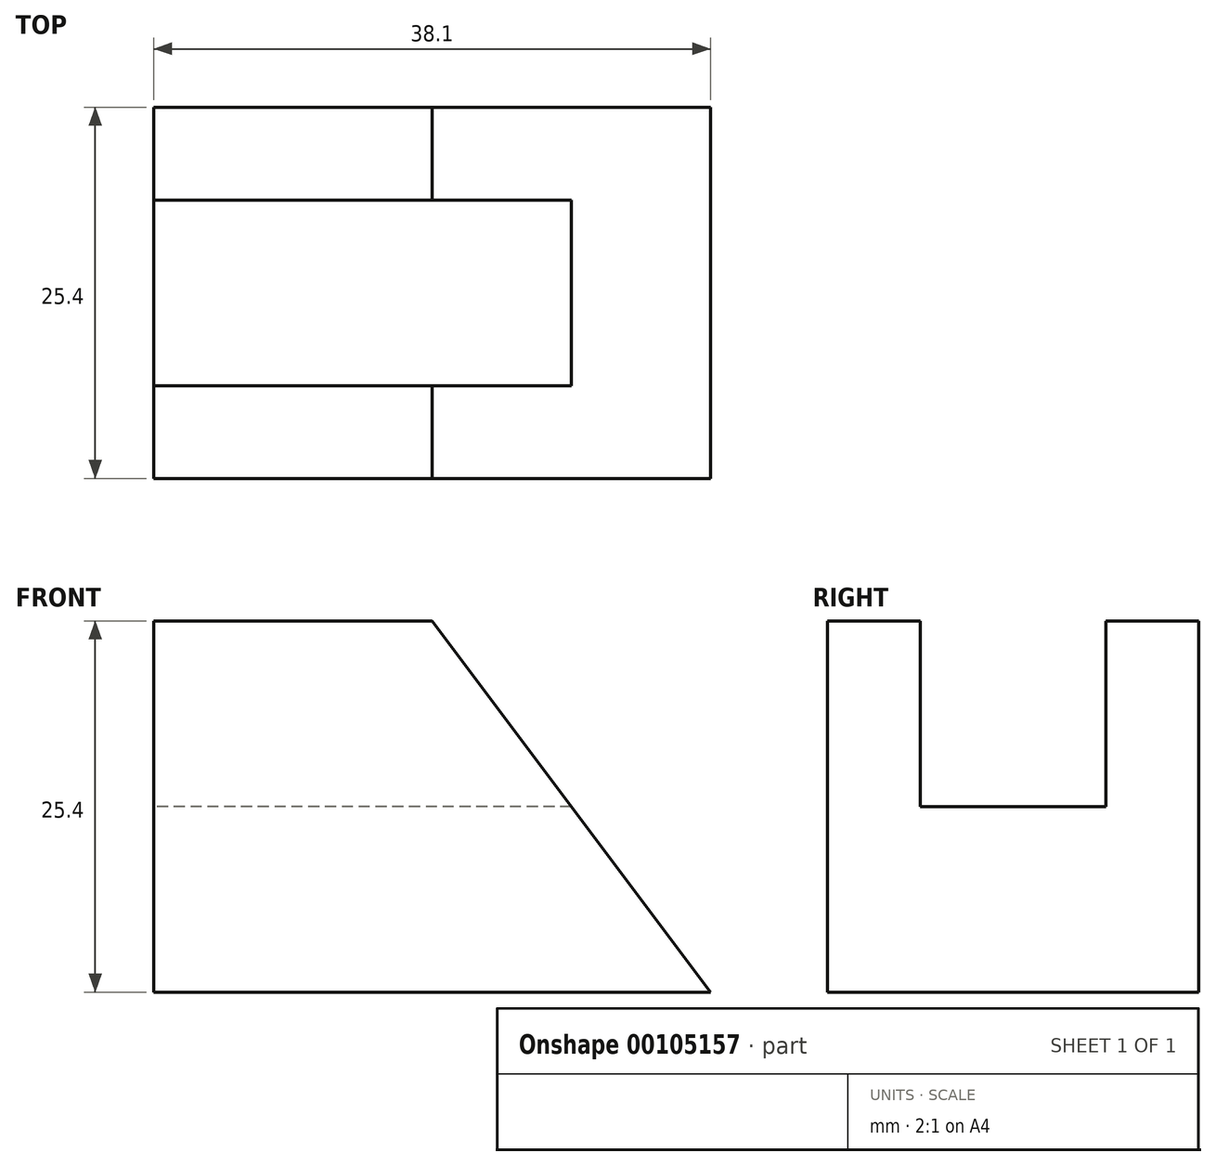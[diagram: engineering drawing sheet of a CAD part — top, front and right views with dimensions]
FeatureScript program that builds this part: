
annotation { "Feature Type Name" : "Feature", "Feature Type Description" : "" }
export const myFeature = defineFeature(function(context is Context, id is Id, definition is map)
    precondition{}
    {
        {
            var Q0;
            Q0=qCreatedBy(makeId("Top.planeOp"),FACE);
            var sketch = newSketch(context, id + "F0", { "sketchPlane" : qUnion([Q0])});
            skLineSegment(sketch, "E0.bottom", {"start": v(0, 0) * mm, "end": v(38.1, 0) * mm});
            skLineSegment(sketch, "E0.top", {"start": v(0, 25.4) * mm, "end": v(38.1, 25.4) * mm});
            skLineSegment(sketch, "E0.left", {"start": v(0, 0) * mm, "end": v(0, 25.4) * mm});
            skLineSegment(sketch, "E0.right", {"start": v(38.1, 0) * mm, "end": v(38.1, 25.4) * mm});
            skSolve(sketch);
        }
        {
            var Q0;
            Q0 = qSketchRegion(id + "F0", true);
            extrude(context, id + "F1", {"entities" : qUnion([Q0]), "endBound" : BoundingType.SYMMETRIC, "depth" : 25.4 * mm});
        }
        {
            var Q0;
            Q0=makeQuery(id+"F1.opExtrude","SWEPT_FACE",FACE,{"disambiguationData":[OSD([sQuery(id+"F0.wireOp",EDGE,"E0.bottom")])]});
            var sketch = newSketch(context, id + "F2", { "sketchPlane" : qUnion([Q0])});
            skLineSegment(sketch, "E1", {"start": v(19.05, 12.7) * mm, "end": v(38.1, -12.7) * mm});
            skSolve(sketch);
        }
        {
            var Q0;
            {var subQ0=sQuery(id+"F2.wireOp",EDGE,"E1");Q0=makeQuery(id+"F2.imprint","IMPRINT",FACE,{"disambiguationData":[TD([[makeQuery(id+"F2.imprint","IMPRINT",EDGE,{"derivedFrom":subQ0}),1.0]])]});}
            extrude(context, id + "F3", {"entities" : qUnion([Q0]), "operationType" : NewBodyOperationType.REMOVE, "endBound" : BoundingType.THROUGH_ALL, "oppositeDirection" : true, "depth" : 25.4 * mm});
        }
        {
            var Q0;
            Q0=makeQuery(id+"F1.opExtrude","SWEPT_FACE",FACE,{"disambiguationData":[OSD([sQuery(id+"F0.wireOp",EDGE,"E0.left")])]});
            var sketch = newSketch(context, id + "F4", { "sketchPlane" : qUnion([Q0])});
            skLineSegment(sketch, "E2.bottom", {"start": v(-19.05, 12.7) * mm, "end": v(-6.35, 12.7) * mm});
            skLineSegment(sketch, "E2.top", {"start": v(-19.05, 0) * mm, "end": v(-6.35, 0) * mm});
            skLineSegment(sketch, "E2.left", {"start": v(-19.05, 12.7) * mm, "end": v(-19.05, 0) * mm});
            skLineSegment(sketch, "E2.right", {"start": v(-6.35, 12.7) * mm, "end": v(-6.35, 0) * mm});
            skPoint(sketch, "E3", {"position": v(-25.4, 0) * mm});
            skSolve(sketch);
        }
        {
            var Q0;
            Q0=makeQuery(id+"F4.imprint","IMPRINT",FACE,{"disambiguationData":[TD([[makeQuery(id+"F4.imprint","IMPRINT",EDGE,{"derivedFrom":sQuery(id+"F4.wireOp",EDGE,"E2.bottom")}),1.0]])]});
            extrude(context, id + "F5", {"entities" : qUnion([Q0]), "operationType" : NewBodyOperationType.REMOVE, "endBound" : BoundingType.THROUGH_ALL, "oppositeDirection" : true, "depth" : 25.4 * mm});
        }
    });
